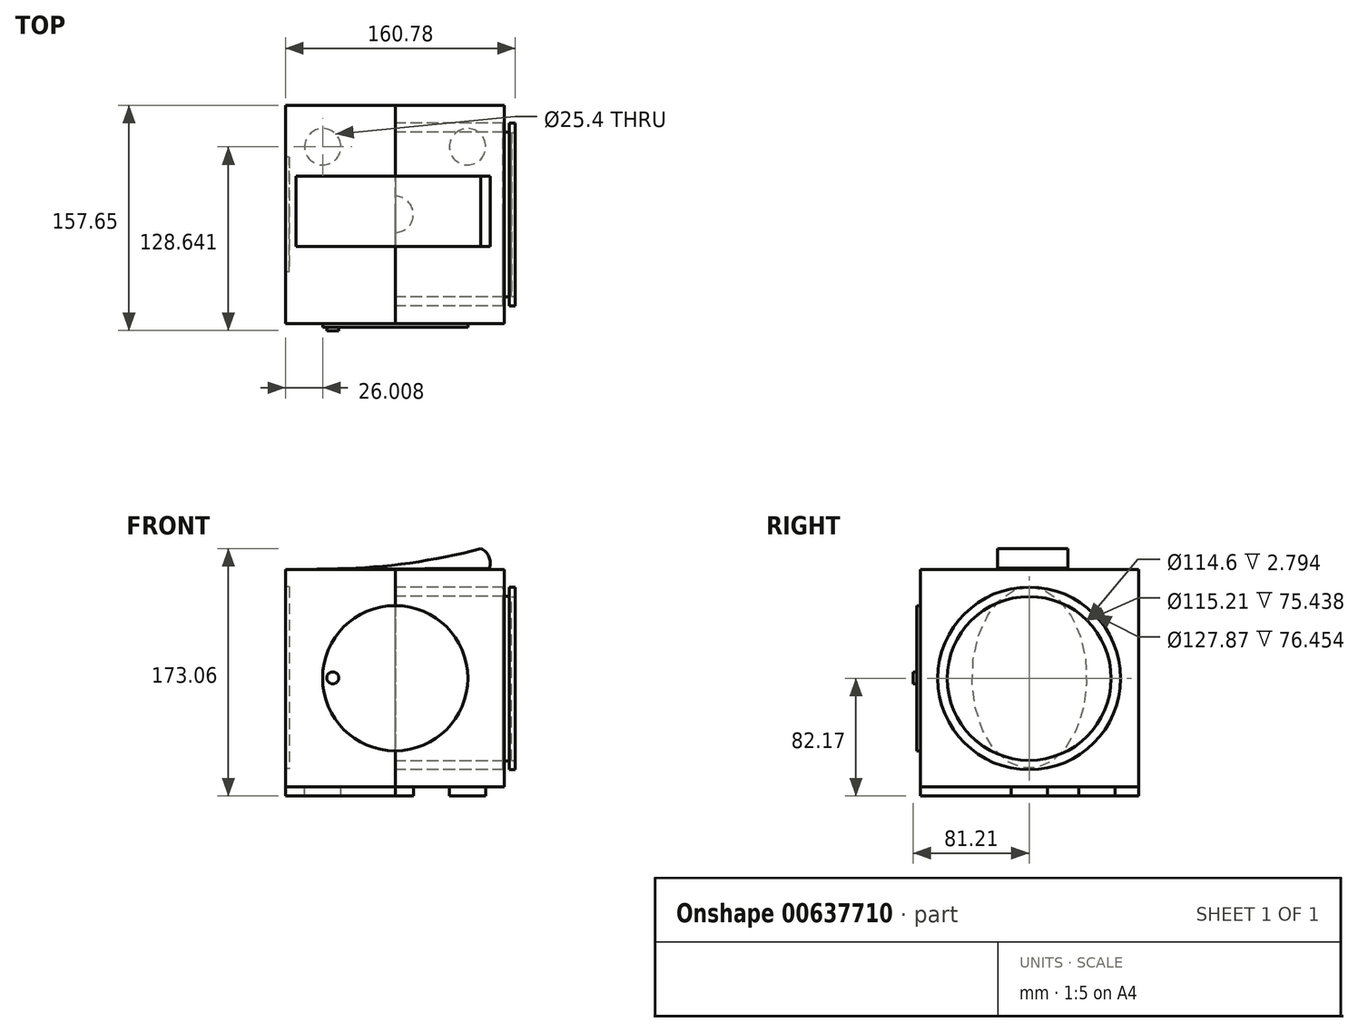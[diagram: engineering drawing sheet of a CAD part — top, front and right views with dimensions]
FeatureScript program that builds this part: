
annotation { "Feature Type Name" : "Feature", "Feature Type Description" : "" }
export const myFeature = defineFeature(function(context is Context, id is Id, definition is map)
    precondition{}
    {
        {
            var Q0;
            Q0=qCreatedBy(makeId("Right.planeOp"),FACE);
            var sketch = newSketch(context, id + "F0", { "sketchPlane" : qUnion([Q0])});
            skCircle(sketch, "E0", {"center": v(0, 0) * mm, "radius": 63.93 * mm});
            skCircle(sketch, "E1", {"center": v(0, 0) * mm, "radius": 57.6 * mm});
            skCircle(sketch, "E2", {"center": v(0, 0) * mm, "radius": 8.34 * mm});
            skCircle(sketch, "E3", {"center": v(0, 0) * mm, "radius": 5.55 * mm});
            skCircle(sketch, "E4", {"center": v(0, 0) * mm, "radius": 3.29 * mm});
            skSolve(sketch);
        }
        {
            var Q0;
            Q0=qCreatedBy(makeId("Right.planeOp"),FACE);
            var sketch = newSketch(context, id + "F1", { "sketchPlane" : qUnion([Q0])});
            skLineSegment(sketch, "E5.bottom", {"start": v(76.44, 76.13) * mm, "end": v(-76.13, 76.13) * mm});
            skLineSegment(sketch, "E5.top", {"start": v(76.44, -75.82) * mm, "end": v(-76.13, -75.82) * mm});
            skLineSegment(sketch, "E5.left", {"start": v(76.44, 76.13) * mm, "end": v(76.44, -75.82) * mm});
            skLineSegment(sketch, "E5.right", {"start": v(-76.13, 76.13) * mm, "end": v(-76.13, -75.82) * mm});
            skSolve(sketch);
        }
        {
            var Q0;
            Q0=makeQuery(id+"F1.imprint","IMPRINT",FACE,{"disambiguationData":[TD([[makeQuery(id+"F1.imprint","IMPRINT",EDGE,{"derivedFrom":sQuery(id+"F1.wireOp",EDGE,"E5.bottom")}),1.0]])]});
            extrude(context, id + "F2", {"entities" : qUnion([Q0]), "depth" : 76.45 * mm, "offsetDistance" : 25.4 * mm});
        }
        {
            var Q0;
            Q0=makeQuery(id+"F0.imprint","IMPRINT",FACE,{"disambiguationData":[TD([[makeQuery(id+"F0.imprint","IMPRINT",EDGE,{"derivedFrom":sQuery(id+"F0.wireOp",EDGE,"E2")}),1.0]])]});
            var Q1;
            Q1=makeQuery(id+"F0.imprint","IMPRINT",FACE,{"disambiguationData":[TD([[makeQuery(id+"F0.imprint","IMPRINT",EDGE,{"derivedFrom":sQuery(id+"F0.wireOp",EDGE,"E0")}),1.0]])]});
            var Q2;
            Q2=makeQuery(id+"F0.imprint","IMPRINT",FACE,{"disambiguationData":[TD([[makeQuery(id+"F0.imprint","IMPRINT",EDGE,{"derivedFrom":sQuery(id+"F0.wireOp",EDGE,"E1")}),1.0]])]});
            var Q3;
            Q3=makeQuery(id+"F0.imprint","IMPRINT",FACE,{"disambiguationData":[TD([[makeQuery(id+"F0.imprint","IMPRINT",EDGE,{"derivedFrom":sQuery(id+"F0.wireOp",EDGE,"E3")}),1.0]])]});
            var Q4;
            Q4=makeQuery(id+"F0.imprint","IMPRINT",FACE,{"disambiguationData":[TD([[makeQuery(id+"F0.imprint","IMPRINT",EDGE,{"derivedFrom":sQuery(id+"F0.wireOp",EDGE,"E4")}),1.0]])]});
            extrude(context, id + "F3", {"entities" : qUnion([Q0, Q1, Q2, Q3, Q4]), "operationType" : NewBodyOperationType.ADD, "depth" : 84.07 * mm, "offsetDistance" : 25.4 * mm});
        }
        {
            var Q0;
            Q0=makeQuery(id+"F0.imprint","IMPRINT",FACE,{"disambiguationData":[TD([[makeQuery(id+"F0.imprint","IMPRINT",EDGE,{"derivedFrom":sQuery(id+"F0.wireOp",EDGE,"E3")}),1.0]])]});
            var Q1;
            Q1=makeQuery(id+"F0.imprint","IMPRINT",FACE,{"disambiguationData":[TD([[makeQuery(id+"F0.imprint","IMPRINT",EDGE,{"derivedFrom":sQuery(id+"F0.wireOp",EDGE,"E4")}),1.0]])]});
            extrude(context, id + "F4", {"entities" : qUnion([Q0, Q1]), "operationType" : NewBodyOperationType.ADD, "depth" : 83.82 * mm, "offsetDistance" : 25.4 * mm});
        }
        {
            var Q0;
            Q0=makeQuery(id+"F0.imprint","IMPRINT",FACE,{"disambiguationData":[TD([[makeQuery(id+"F0.imprint","IMPRINT",EDGE,{"derivedFrom":sQuery(id+"F0.wireOp",EDGE,"E0")}),1.0]])]});
            extrude(context, id + "F5", {"entities" : qUnion([Q0]), "operationType" : NewBodyOperationType.REMOVE, "depth" : 79.76 * mm, "offsetDistance" : 25.4 * mm});
        }
        {
            var Q0;
            Q0=makeQuery(id+"F0.imprint","IMPRINT",FACE,{"disambiguationData":[TD([[makeQuery(id+"F0.imprint","IMPRINT",EDGE,{"derivedFrom":sQuery(id+"F0.wireOp",EDGE,"E0")}),1.0]])]});
            extrude(context, id + "F6", {"entities" : qUnion([Q0]), "depth" : 75.44 * mm, "offsetDistance" : 25.4 * mm});
        }
        {
            var Q0;
            Q0=makeQuery(id+"F1.imprint","IMPRINT",FACE,{"disambiguationData":[TD([[makeQuery(id+"F1.imprint","IMPRINT",EDGE,{"derivedFrom":sQuery(id+"F1.wireOp",EDGE,"E5.bottom")}),1.0]])]});
            extrude(context, id + "F7", {"entities" : qUnion([Q0]), "oppositeDirection" : true, "depth" : 76.7 * mm, "offsetDistance" : 25.4 * mm});
        }
        {
            var Q0;
            Q0=makeQuery(id+"F7.opExtrude","SWEPT_FACE",FACE,{"disambiguationData":[OSD([sQuery(id+"F1.wireOp",EDGE,"E5.right")])]});
            var sketch = newSketch(context, id + "F8", { "sketchPlane" : qUnion([Q0])});
            skCircle(sketch, "E6", {"center": v(0, 0.16) * mm, "radius": 50.8 * mm});
            skCircle(sketch, "E7", {"center": v(-43.26, 0.16) * mm, "radius": 3.78 * mm});
            skSolve(sketch);
        }
        {
            var Q0;
            Q0=makeQuery(id+"F8.imprint","IMPRINT",FACE,{"disambiguationData":[TD([[makeQuery(id+"F8.imprint","IMPRINT",EDGE,{"derivedFrom":sQuery(id+"F8.wireOp",EDGE,"E7")}),1.0]])]});
            var Q1;
            Q1=makeQuery(id+"F8.imprint","IMPRINT",FACE,{"disambiguationData":[TD([[makeQuery(id+"F8.imprint","IMPRINT",EDGE,{"derivedFrom":sQuery(id+"F8.wireOp",EDGE,"E7")}),-1.0]])]});
            var Q2;
            {var subQ0=sQuery(id+"F8.wireOp",EDGE,"E6");var subQ1=makeQuery(id+"F7.opExtrude","CAP_EDGE",EDGE,{"disambiguationData":[OSD([sQuery(id+"F1.wireOp",EDGE,"E5.right")])],"isStart":true});var subQ2=makeQuery(id+"F8.imprint","INTERSECT",VERTEX,{"disambiguationData":[OD(0.0)],"derivedFrom":[subQ1,subQ0]});Q2=makeQuery(id+"F8.imprint","IMPRINT",FACE,{"disambiguationData":[TD([[makeQuery(id+"F8.imprint","IMPRINT",EDGE,{"disambiguationData":[TD([[subQ2,1.0]])],"derivedFrom":subQ0}),1.0]])]});}
            extrude(context, id + "F9", {"entities" : qUnion([Q0, Q1, Q2]), "depth" : 2.54 * mm, "offsetDistance" : 25.4 * mm});
        }
        {
            var Q0;
            Q0=makeQuery(id+"F9.opExtrude","CAP_FACE",FACE,{"disambiguationData":[OSD([sQuery(id+"F8.wireOp",EDGE,"E6")])],"isStart":false});
            var sketch = newSketch(context, id + "F10", { "sketchPlane" : qUnion([Q0])});
            skCircle(sketch, "E8", {"center": v(-43.68, 0.41) * mm, "radius": 4.21 * mm});
            skSolve(sketch);
        }
        {
            var Q0;
            Q0=makeQuery(id+"F10.imprint","IMPRINT",FACE,{"disambiguationData":[TD([[makeQuery(id+"F10.imprint","IMPRINT",EDGE,{"derivedFrom":sQuery(id+"F10.wireOp",EDGE,"E8")}),1.0]])]});
            extrude(context, id + "F11", {"entities" : qUnion([Q0]), "operationType" : NewBodyOperationType.ADD, "depth" : 2.54 * mm, "offsetDistance" : 25.4 * mm});
        }
        {
            var Q0;
            {var subQ0=sQuery(id+"F1.wireOp",EDGE,"E5.right");Q0=makeQuery(id+"F8.imprint","IMPRINT",FACE,{"disambiguationData":[TD([[makeQuery(id+"F8.imprint","IMPRINT",EDGE,{"derivedFrom":makeQuery(id+"F7.opExtrude","CAP_EDGE",EDGE,{"disambiguationData":[OSD([subQ0])],"isStart":false})}),1.0]])]});}
            var sketch = newSketch(context, id + "F12", { "sketchPlane" : qUnion([Q0])});
            skArc(sketch, "E9", {"start": v(65.93, 77.24) * mm, "mid": v(65.63, 85.24) * mm, "end": v(59.95, 90.9) * mm});
            skArc(sketch, "E10", {"start": v(-40.33, 76.8) * mm, "mid": v(10.25, 80.79) * mm, "end": v(59.95, 90.9) * mm});
            skLineSegment(sketch, "E11", {"start": v(-40.33, 76.8) * mm, "end": v(-69.32, 76.3) * mm});
            skLineSegment(sketch, "E12", {"start": v(-69.32, 76.3) * mm, "end": v(65.93, 77.24) * mm});
            skSolve(sketch);
        }
        {
            var Q0;
            Q0=makeQuery(id+"F12.imprint","IMPRINT",FACE,{"disambiguationData":[TD([[makeQuery(id+"F12.imprint","IMPRINT",EDGE,{"derivedFrom":sQuery(id+"F12.wireOp",EDGE,"E9")}),1.0]])]});
            extrude(context, id + "F13", {"entities" : qUnion([Q0]), "oppositeDirection" : true, "depth" : 103.12 * mm, "offsetDistance" : 25.4 * mm});
        }
        {
            var Q0;
            Q0=makeQuery(id+"F13.opExtrude","CAP_FACE",FACE,{"disambiguationData":[OSD([sQuery(id+"F12.wireOp",EDGE,"E9"),sQuery(id+"F12.wireOp",EDGE,"E10"),sQuery(id+"F12.wireOp",EDGE,"E11"),sQuery(id+"F12.wireOp",EDGE,"E12")])],"isStart":true});
            extrude(context, id + "F14", {"entities" : qUnion([Q0]), "operationType" : NewBodyOperationType.REMOVE, "oppositeDirection" : true, "depth" : 53.85 * mm, "offsetDistance" : 25.4 * mm});
        }
        {
            var Q0;
            Q0=makeQuery(id+"F7.opExtrude","SWEPT_FACE",FACE,{"disambiguationData":[OSD([sQuery(id+"F1.wireOp",EDGE,"E5.top")])]});
            var sketch = newSketch(context, id + "F15", { "sketchPlane" : qUnion([Q0])});
            skCircle(sketch, "E13", {"center": v(0, -0.16) * mm, "radius": 12.7 * mm});
            skCircle(sketch, "E14", {"center": v(-50.7, 47.43) * mm, "radius": 12.7 * mm});
            skCircle(sketch, "E15.MirrorC", {"center": v(50.7, 47.43) * mm, "radius": 12.7 * mm});
            skCircle(sketch, "E16.MirrorC", {"center": v(-50.7, -47.43) * mm, "radius": 12.7 * mm});
            skCircle(sketch, "E17.MirrorC", {"center": v(50.7, -47.43) * mm, "radius": 12.7 * mm});
            skSolve(sketch);
        }
        {
            var Q0;
            Q0=makeQuery(id+"F15.imprint","IMPRINT",FACE,{"disambiguationData":[TD([[makeQuery(id+"F15.imprint","IMPRINT",EDGE,{"derivedFrom":sQuery(id+"F15.wireOp",EDGE,"E14")}),1.0]])]});
            var Q1;
            {var subQ0=sQuery(id+"F15.wireOp",EDGE,"E13");var subQ1=makeQuery(id+"F7.opExtrude","CAP_EDGE",EDGE,{"disambiguationData":[OSD([sQuery(id+"F1.wireOp",EDGE,"E5.top")])],"isStart":true});var subQ2=makeQuery(id+"F15.imprint","INTERSECT",VERTEX,{"disambiguationData":[OD(0.0)],"derivedFrom":[subQ1,subQ0]});Q1=makeQuery(id+"F15.imprint","IMPRINT",FACE,{"disambiguationData":[TD([[makeQuery(id+"F15.imprint","IMPRINT",EDGE,{"disambiguationData":[TD([[subQ2,1.0]])],"derivedFrom":subQ0}),1.0]])]});}
            var Q2;
            {var subQ0=sQuery(id+"F15.wireOp",EDGE,"E13");var subQ1=makeQuery(id+"F7.opExtrude","CAP_EDGE",EDGE,{"disambiguationData":[OSD([sQuery(id+"F1.wireOp",EDGE,"E5.top")])],"isStart":true});var subQ2=makeQuery(id+"F15.imprint","INTERSECT",VERTEX,{"disambiguationData":[OD(0.0)],"derivedFrom":[subQ1,subQ0]});Q2=makeQuery(id+"F15.imprint","IMPRINT",FACE,{"disambiguationData":[TD([[makeQuery(id+"F15.imprint","IMPRINT",EDGE,{"disambiguationData":[TD([[subQ2,-1.0]])],"derivedFrom":subQ0}),1.0]])]});}
            var Q3;
            Q3=makeQuery(id+"F15.imprint","IMPRINT",FACE,{"disambiguationData":[TD([[makeQuery(id+"F15.imprint","IMPRINT",EDGE,{"derivedFrom":sQuery(id+"F15.wireOp",EDGE,"E15.MirrorC")}),-1.0]])]});
            var Q4;
            Q4=makeQuery(id+"F15.imprint","IMPRINT",FACE,{"disambiguationData":[TD([[makeQuery(id+"F15.imprint","IMPRINT",EDGE,{"derivedFrom":sQuery(id+"F15.wireOp",EDGE,"E17.MirrorC")}),1.0]])]});
            var Q5;
            Q5=makeQuery(id+"F15.imprint","IMPRINT",FACE,{"disambiguationData":[TD([[makeQuery(id+"F15.imprint","IMPRINT",EDGE,{"derivedFrom":sQuery(id+"F15.wireOp",EDGE,"E16.MirrorC")}),-1.0]])]});
            extrude(context, id + "F16", {"entities" : qUnion([Q0, Q1, Q2, Q3, Q4, Q5]), "depth" : 6.35 * mm, "offsetDistance" : 25.4 * mm});
        }
        {
            var Q0;
            Q0=makeQuery(id+"F7.opExtrude","CAP_FACE",FACE,{"disambiguationData":[OSD([sQuery(id+"F1.wireOp",EDGE,"E5.bottom"),sQuery(id+"F1.wireOp",EDGE,"E5.top"),sQuery(id+"F1.wireOp",EDGE,"E5.left"),sQuery(id+"F1.wireOp",EDGE,"E5.right")])],"isStart":false});
            var sketch = newSketch(context, id + "F17", { "sketchPlane" : qUnion([Q0])});
            skEllipse(sketch, "E18", {"center": v(-0.12, 0.5) * mm, "majorRadius": 63.52 * mm, "minorRadius": 40.09 * mm, "majorAxis": v(0, 1)});
            skSolve(sketch);
        }
        {
            var Q0;
            Q0=makeQuery(id+"F17.imprint","IMPRINT",FACE,{"disambiguationData":[TD([[makeQuery(id+"F17.imprint","IMPRINT",EDGE,{"derivedFrom":sQuery(id+"F17.wireOp",EDGE,"E18")}),1.0]])]});
            extrude(context, id + "F18", {"entities" : qUnion([Q0]), "operationType" : NewBodyOperationType.REMOVE, "oppositeDirection" : true, "depth" : 2.54 * mm, "offsetDistance" : 25.4 * mm});
        }
        {
            var Q0;
            Q0=makeQuery(id+"F3.opExtrude","CAP_FACE",FACE,{"disambiguationData":[OSD([sQuery(id+"F0.wireOp",EDGE,"E0")])],"isStart":false});
            var sketch = newSketch(context, id + "F19", { "sketchPlane" : qUnion([Q0])});
            skCircle(sketch, "E19", {"center": v(0, 0) * mm, "radius": 57.3 * mm});
            skSolve(sketch);
        }
        {
            var Q0;
            Q0=makeQuery(id+"F19.imprint","IMPRINT",FACE,{"disambiguationData":[TD([[makeQuery(id+"F19.imprint","IMPRINT",EDGE,{"derivedFrom":sQuery(id+"F19.wireOp",EDGE,"E19")}),1.0]])]});
            extrude(context, id + "F20", {"entities" : qUnion([Q0]), "operationType" : NewBodyOperationType.REMOVE, "oppositeDirection" : true, "depth" : 2.8 * mm, "offsetDistance" : 25.4 * mm});
        }
        {
            var Q0;
            Q0=makeQuery(id+"F2.opExtrude","SWEPT_FACE",FACE,{"disambiguationData":[OSD([sQuery(id+"F1.wireOp",EDGE,"E5.left")])]});
            var sketch = newSketch(context, id + "F21", { "sketchPlane" : qUnion([Q0])});
            skLineSegment(sketch, "E20", {"start": v(0, 58.9) * mm, "end": v(-4.66, 58.9) * mm});
            skLineSegment(sketch, "E21", {"start": v(-4.66, 58.9) * mm, "end": v(0, 58.9) * mm});
            skLineSegment(sketch, "E22", {"start": v(0, 58.9) * mm, "end": v(4.67, 58.9) * mm});
            skLineSegment(sketch, "E23", {"start": v(-4.66, 58.9) * mm, "end": v(-4.66, 38.58) * mm});
            skLineSegment(sketch, "E24", {"start": v(-4.66, 38.58) * mm, "end": v(4.67, 38.58) * mm});
            skLineSegment(sketch, "E25", {"start": v(4.67, 38.58) * mm, "end": v(4.67, 58.9) * mm});
            skLineSegment(sketch, "E26", {"start": v(4.67, 48.74) * mm, "end": v(-4.66, 48.74) * mm});
            skLineSegment(sketch, "E27", {"start": v(-4.66, 48.74) * mm, "end": v(-4.66, 43.66) * mm});
            skLineSegment(sketch, "E28", {"start": v(-4.66, 43.66) * mm, "end": v(4.67, 43.66) * mm});
            skLineSegment(sketch, "E29", {"start": v(4.67, 43.66) * mm, "end": v(4.67, 48.74) * mm});
            skLineSegment(sketch, "E30", {"start": v(-4.66, 48.74) * mm, "end": v(-4.66, 53.82) * mm});
            skLineSegment(sketch, "E31", {"start": v(-4.66, 53.82) * mm, "end": v(4.67, 53.82) * mm});
            skLineSegment(sketch, "E32", {"start": v(-4.66, 58.9) * mm, "end": v(4.67, 58.9) * mm});
            skLineSegment(sketch, "E33", {"start": v(-14.01, 58.9) * mm, "end": v(-23.36, 58.9) * mm});
            skLineSegment(sketch, "E34", {"start": v(-23.36, 58.9) * mm, "end": v(-23.36, 38.58) * mm});
            skLineSegment(sketch, "E35", {"start": v(-23.36, 38.58) * mm, "end": v(-14.01, 38.58) * mm});
            skLineSegment(sketch, "E36", {"start": v(-14.01, 38.58) * mm, "end": v(-14.01, 43.66) * mm});
            skLineSegment(sketch, "E37", {"start": v(-14.01, 43.66) * mm, "end": v(-14.01, 48.74) * mm});
            skLineSegment(sketch, "E38", {"start": v(-14.01, 48.74) * mm, "end": v(-14.01, 53.82) * mm});
            skLineSegment(sketch, "E39", {"start": v(-14.01, 53.82) * mm, "end": v(-14.01, 58.9) * mm});
            skLineSegment(sketch, "E40", {"start": v(-14.01, 53.82) * mm, "end": v(-23.36, 53.82) * mm});
            skLineSegment(sketch, "E41", {"start": v(-23.36, 53.82) * mm, "end": v(-23.36, 48.74) * mm});
            skLineSegment(sketch, "E42", {"start": v(-23.36, 48.74) * mm, "end": v(-14.01, 48.74) * mm});
            skLineSegment(sketch, "E43", {"start": v(-14.01, 43.66) * mm, "end": v(-23.36, 43.66) * mm});
            skLineSegment(sketch, "E44.MirrorCS", {"start": v(14.01, 58.9) * mm, "end": v(23.36, 58.9) * mm});
            skLineSegment(sketch, "E45.MirrorCS", {"start": v(23.36, 58.9) * mm, "end": v(23.36, 38.58) * mm});
            skLineSegment(sketch, "E46.MirrorCS", {"start": v(14.01, 53.82) * mm, "end": v(14.01, 58.9) * mm});
            skLineSegment(sketch, "E47.MirrorCS", {"start": v(14.01, 48.74) * mm, "end": v(14.01, 53.82) * mm});
            skLineSegment(sketch, "E48.MirrorCS", {"start": v(14.01, 53.82) * mm, "end": v(23.36, 53.82) * mm});
            skLineSegment(sketch, "E49.MirrorCS", {"start": v(23.36, 53.82) * mm, "end": v(23.36, 48.74) * mm});
            skLineSegment(sketch, "E50.MirrorCS", {"start": v(23.36, 38.58) * mm, "end": v(14.01, 38.58) * mm});
            skLineSegment(sketch, "E51.MirrorCS", {"start": v(14.01, 38.58) * mm, "end": v(14.01, 43.66) * mm});
            skLineSegment(sketch, "E52.MirrorCS", {"start": v(14.01, 43.66) * mm, "end": v(23.36, 43.66) * mm});
            skLineSegment(sketch, "E53.MirrorCS", {"start": v(14.01, 43.66) * mm, "end": v(14.01, 48.74) * mm});
            skLineSegment(sketch, "E54.MirrorCS", {"start": v(23.36, 48.74) * mm, "end": v(14.01, 48.74) * mm});
            skLineSegment(sketch, "E55.MirrorCS", {"start": v(0, 58.9) * mm, "end": v(4.66, 58.9) * mm});
            skLineSegment(sketch, "E56.MirrorCS", {"start": v(4.66, 58.9) * mm, "end": v(0, 58.9) * mm});
            skLineSegment(sketch, "E57.MirrorCS", {"start": v(0, 58.9) * mm, "end": v(-4.67, 58.9) * mm});
            skLineSegment(sketch, "E58.MirrorCS", {"start": v(4.66, 58.9) * mm, "end": v(-4.67, 58.9) * mm});
            skLineSegment(sketch, "E59.MirrorCS", {"start": v(4.66, 48.74) * mm, "end": v(4.66, 43.66) * mm});
            skLineSegment(sketch, "E60.MirrorCS", {"start": v(-4.67, 43.66) * mm, "end": v(-4.67, 48.74) * mm});
            skLineSegment(sketch, "E61.MirrorCS", {"start": v(4.66, 58.9) * mm, "end": v(4.66, 38.58) * mm});
            skLineSegment(sketch, "E62.MirrorCS", {"start": v(4.66, 38.58) * mm, "end": v(-4.67, 38.58) * mm});
            skLineSegment(sketch, "E63.MirrorCS", {"start": v(-4.67, 38.58) * mm, "end": v(-4.67, 58.9) * mm});
            skLineSegment(sketch, "E64.MirrorCS", {"start": v(-4.67, 48.74) * mm, "end": v(4.66, 48.74) * mm});
            skLineSegment(sketch, "E65.MirrorCS", {"start": v(4.66, 43.66) * mm, "end": v(-4.67, 43.66) * mm});
            skLineSegment(sketch, "E66.MirrorCS", {"start": v(4.66, 48.74) * mm, "end": v(4.66, 53.82) * mm});
            skLineSegment(sketch, "E67.MirrorCS", {"start": v(4.66, 53.82) * mm, "end": v(-4.67, 53.82) * mm});
            skLineSegment(sketch, "E68", {"start": v(-4.66, 38.58) * mm, "end": v(0, 38.58) * mm});
            skLineSegment(sketch, "E69", {"start": v(0, -18.62) * mm, "end": v(0, -66.48) * mm});
            skCircle(sketch, "E70", {"center": v(0, -18.62) * mm, "radius": 47.86 * mm});
            skPoint(sketch, "E71.end.orphan", {"position": v(0, 29.24) * mm});
            skSolve(sketch);
        }
        {
            var Q0;
            {var subQ0=sQuery(id+"F21.wireOp",EDGE,"E69");Q0=makeQuery(id+"F21.imprint","IMPRINT",FACE,{"disambiguationData":[TD([[makeQuery(id+"F21.imprint","IMPRINT",EDGE,{"derivedFrom":subQ0}),1.0]])]});}
            cPlane(context, id + "F22", {"entities" : qUnion([Q0]), "cplaneType" : CPlaneType.OFFSET, "offset" : 25.4 * mm, "width" : 152.4 * mm, "height" : 152.4 * mm});
        }
    });
